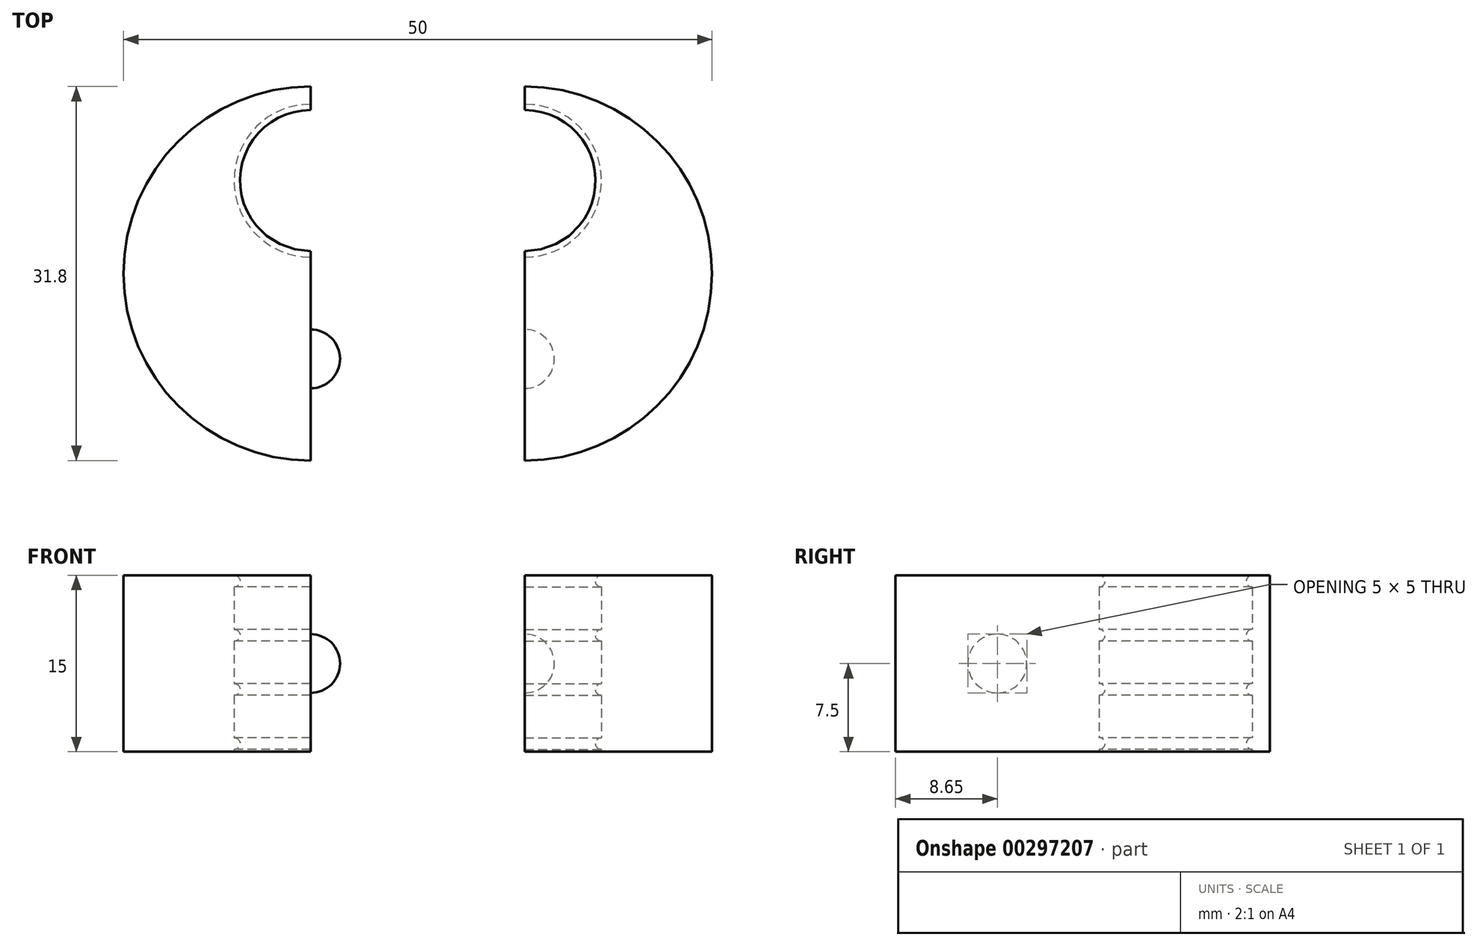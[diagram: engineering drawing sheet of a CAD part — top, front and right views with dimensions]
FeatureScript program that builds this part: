
annotation { "Feature Type Name" : "Feature", "Feature Type Description" : "" }
export const myFeature = defineFeature(function(context is Context, id is Id, definition is map)
    precondition{}
    {
        {
            var Q0;
            Q0=qCreatedBy(makeId("Top.planeOp"),FACE);
            var sketch = newSketch(context, id + "F0", { "sketchPlane" : qUnion([Q0])});
            skArc(sketch, "E0", {"start": v(-8.12, 15.9) * mm, "mid": v(-24.02, 0) * mm, "end": v(-8.12, -15.9) * mm});
            skArc(sketch, "E1", {"start": v(10.08, -15.9) * mm, "mid": v(25.98, 0) * mm, "end": v(10.08, 15.9) * mm});
            skLineSegment(sketch, "E2", {"start": v(-8.12, 15.9) * mm, "end": v(-8.12, 14.4) * mm});
            skLineSegment(sketch, "E3", {"start": v(10.08, 15.9) * mm, "end": v(10.08, 14.4) * mm});
            skArc(sketch, "E4", {"start": v(-8.12, 14.4) * mm, "mid": v(-14.62, 7.9) * mm, "end": v(-8.12, 1.4) * mm});
            skArc(sketch, "E5", {"start": v(10.08, 1.4) * mm, "mid": v(16.58, 7.9) * mm, "end": v(10.08, 14.4) * mm});
            skLineSegment(sketch, "E6.trimOffspring", {"start": v(-8.12, 1.4) * mm, "end": v(-8.12, -15.9) * mm});
            skLineSegment(sketch, "E7.trimOffspring", {"start": v(10.08, 1.4) * mm, "end": v(10.08, -15.9) * mm});
            skSolve(sketch);
        }
        {
            var Q0;
            Q0=makeQuery(id+"F0.imprint","IMPRINT",FACE,{"disambiguationData":[TD([[makeQuery(id+"F0.imprint","IMPRINT",EDGE,{"derivedFrom":sQuery(id+"F0.wireOp",EDGE,"E0")}),1.0]])]});
            var Q1;
            Q1=makeQuery(id+"F0.imprint","IMPRINT",FACE,{"disambiguationData":[TD([[makeQuery(id+"F0.imprint","IMPRINT",EDGE,{"derivedFrom":sQuery(id+"F0.wireOp",EDGE,"E1")}),1.0]])]});
            extrude(context, id + "F1", {"entities" : qUnion([Q0, Q1]), "depth" : 15 * mm});
        }
        {
            var Q0;
            Q0=makeQuery(id+"F1.opExtrude","SWEPT_FACE",FACE,{"disambiguationData":[OSD([sQuery(id+"F0.wireOp",EDGE,"E6.trimOffspring")])]});
            var sketch = newSketch(context, id + "F2", { "sketchPlane" : qUnion([Q0])});
            skArc(sketch, "E8", {"start": v(-7.25, 5) * mm, "mid": v(-4.75, 7.5) * mm, "end": v(-7.25, 10) * mm});
            skPoint(sketch, "E8.centerSnap0", {"position": v(1.4, 7.5) * mm});
            skPoint(sketch, "E8.centerSnap1", {"position": v(-7.25, 15) * mm});
            skLineSegment(sketch, "E9", {"start": v(-7.25, 10) * mm, "end": v(-7.25, 5) * mm});
            skLineSegment(sketch, "E10", {"start": v(-7.25, 15) * mm, "end": v(-7.25, 0) * mm, "construction": true});
            skSolve(sketch);
        }
        {
            var Q0;
            Q0=makeQuery(id+"F2.imprint","IMPRINT",FACE,{"disambiguationData":[TD([[makeQuery(id+"F2.imprint","IMPRINT",EDGE,{"derivedFrom":sQuery(id+"F2.wireOp",EDGE,"E8")}),1.0]])]});
            var Q1;
            Q1=sQuery(id+"F2.wireOp",EDGE,"E10");
            revolve(context, id + "F3", {"operationType" : NewBodyOperationType.ADD, "entities" : qUnion([Q0]), "axis" : qUnion([Q1]), "revolveType" : RevolveType.FULL});
        }
        {
            var Q0;
            Q0=makeQuery(id+"F1.opExtrude","SWEPT_FACE",FACE,{"disambiguationData":[OSD([sQuery(id+"F0.wireOp",EDGE,"E7.trimOffspring")])]});
            var sketch = newSketch(context, id + "F4", { "sketchPlane" : qUnion([Q0])});
            skArc(sketch, "E11", {"start": v(7.25, 10) * mm, "mid": v(4.75, 7.5) * mm, "end": v(7.25, 5) * mm});
            skPoint(sketch, "E11.centerSnap0", {"position": v(-1.4, 7.5) * mm});
            skPoint(sketch, "E11.centerSnap1", {"position": v(7.25, 0) * mm});
            skLineSegment(sketch, "E12", {"start": v(7.25, 0) * mm, "end": v(7.25, 15) * mm, "construction": true});
            skLineSegment(sketch, "E13", {"start": v(7.25, 5) * mm, "end": v(7.25, 10) * mm});
            skSolve(sketch);
        }
        {
            var Q0;
            Q0=makeQuery(id+"F4.imprint","IMPRINT",FACE,{"disambiguationData":[TD([[makeQuery(id+"F4.imprint","IMPRINT",EDGE,{"derivedFrom":sQuery(id+"F4.wireOp",EDGE,"E11")}),1.0]])]});
            var Q1;
            Q1=sQuery(id+"F4.wireOp",EDGE,"E12");
            revolve(context, id + "F5", {"operationType" : NewBodyOperationType.REMOVE, "entities" : qUnion([Q0]), "axis" : qUnion([Q1]), "revolveType" : RevolveType.FULL, "oppositeDirection" : true});
        }
        {
            var Q0;
            Q0=makeQuery(id+"F1.opExtrude","SWEPT_FACE",FACE,{"disambiguationData":[OSD([sQuery(id+"F0.wireOp",EDGE,"E6.trimOffspring")])]});
            var sketch = newSketch(context, id + "F6", { "sketchPlane" : qUnion([Q0])});
            skArc(sketch, "E14", {"start": v(1.4, 14) * mm, "mid": v(1.9, 14.5) * mm, "end": v(1.4, 15) * mm});
            skArc(sketch, "E15.1.0.0", {"start": v(1.4, 9.4) * mm, "mid": v(1.9, 9.9) * mm, "end": v(1.4, 10.4) * mm});
            skArc(sketch, "E15.2.0.0", {"start": v(1.4, 4.8) * mm, "mid": v(1.9, 5.3) * mm, "end": v(1.4, 5.8) * mm});
            skArc(sketch, "E15.3.0.0", {"start": v(1.4, 0.2) * mm, "mid": v(1.9, 0.7) * mm, "end": v(1.4, 1.2) * mm});
            skLineSegment(sketch, "E15.direction1", {"start": v(1.4, 14) * mm, "end": v(1.4, 9.4) * mm, "construction": true});
            skSolve(sketch);
        }
        {
            var Q0;
            {var subQ0=sQuery(id+"F6.wireOp",EDGE,"E14");Q0=makeQuery(id+"F6.imprint","IMPRINT",FACE,{"disambiguationData":[TD([[makeQuery(id+"F6.imprint","IMPRINT",EDGE,{"derivedFrom":subQ0}),1.0]])]});}
            var Q1;
            {var subQ0=sQuery(id+"F6.wireOp",EDGE,"E15.1.0.0");Q1=makeQuery(id+"F6.imprint","IMPRINT",FACE,{"disambiguationData":[TD([[makeQuery(id+"F6.imprint","IMPRINT",EDGE,{"derivedFrom":subQ0}),1.0]])]});}
            var Q2;
            {var subQ0=sQuery(id+"F6.wireOp",EDGE,"E15.2.0.0");Q2=makeQuery(id+"F6.imprint","IMPRINT",FACE,{"disambiguationData":[TD([[makeQuery(id+"F6.imprint","IMPRINT",EDGE,{"derivedFrom":subQ0}),1.0]])]});}
            var Q3;
            {var subQ0=sQuery(id+"F6.wireOp",EDGE,"E15.3.0.0");Q3=makeQuery(id+"F6.imprint","IMPRINT",FACE,{"disambiguationData":[TD([[makeQuery(id+"F6.imprint","IMPRINT",EDGE,{"derivedFrom":subQ0}),1.0]])]});}
            var Q4;
            Q4=makeQuery(id+"F1.opExtrude","SWEPT_FACE",FACE,{"disambiguationData":[OSD([sQuery(id+"F0.wireOp",EDGE,"E4")])]});
            revolve(context, id + "F7", {"operationType" : NewBodyOperationType.ADD, "entities" : qUnion([Q0, Q1, Q2, Q3]), "axis" : qUnion([Q4]), "revolveType" : RevolveType.ONE_DIRECTION, "oppositeDirection" : true, "angle" : 180 * degree});
        }
        {
            var Q0;
            Q0=makeQuery(id+"F1.opExtrude","SWEPT_FACE",FACE,{"disambiguationData":[OSD([sQuery(id+"F0.wireOp",EDGE,"E7.trimOffspring")])]});
            var sketch = newSketch(context, id + "F8", { "sketchPlane" : qUnion([Q0])});
            skArc(sketch, "E16", {"start": v(-1.4, 15) * mm, "mid": v(-1.9, 14.5) * mm, "end": v(-1.4, 14) * mm});
            skArc(sketch, "E17.0.1.0", {"start": v(-1.4, 10.4) * mm, "mid": v(-1.9, 9.9) * mm, "end": v(-1.4, 9.4) * mm});
            skArc(sketch, "E17.0.2.0", {"start": v(-1.4, 5.8) * mm, "mid": v(-1.9, 5.3) * mm, "end": v(-1.4, 4.8) * mm});
            skArc(sketch, "E17.0.3.0", {"start": v(-1.4, 1.2) * mm, "mid": v(-1.9, 0.7) * mm, "end": v(-1.4, 0.2) * mm});
            skArc(sketch, "E17.1.0.0", {"start": v(23.6, 15) * mm, "mid": v(23.1, 14.5) * mm, "end": v(23.6, 14) * mm});
            skArc(sketch, "E17.1.1.0", {"start": v(23.6, 10.4) * mm, "mid": v(23.1, 9.9) * mm, "end": v(23.6, 9.4) * mm});
            skArc(sketch, "E17.1.2.0", {"start": v(23.6, 5.8) * mm, "mid": v(23.1, 5.3) * mm, "end": v(23.6, 4.8) * mm});
            skArc(sketch, "E17.1.3.0", {"start": v(23.6, 1.2) * mm, "mid": v(23.1, 0.7) * mm, "end": v(23.6, 0.2) * mm});
            skArc(sketch, "E17.2.0.0", {"start": v(48.6, 15) * mm, "mid": v(48.1, 14.5) * mm, "end": v(48.6, 14) * mm});
            skArc(sketch, "E17.2.1.0", {"start": v(48.6, 10.4) * mm, "mid": v(48.1, 9.9) * mm, "end": v(48.6, 9.4) * mm});
            skArc(sketch, "E17.2.2.0", {"start": v(48.6, 5.8) * mm, "mid": v(48.1, 5.3) * mm, "end": v(48.6, 4.8) * mm});
            skArc(sketch, "E17.2.3.0", {"start": v(48.6, 1.2) * mm, "mid": v(48.1, 0.7) * mm, "end": v(48.6, 0.2) * mm});
            skLineSegment(sketch, "E17.direction1", {"start": v(-1.4, 14) * mm, "end": v(23.6, 14) * mm, "construction": true});
            skLineSegment(sketch, "E17.direction2", {"start": v(-1.4, 14) * mm, "end": v(-1.4, 9.4) * mm, "construction": true});
            skSolve(sketch);
        }
        {
            var Q0;
            {var subQ0=sQuery(id+"F8.wireOp",EDGE,"E16");Q0=makeQuery(id+"F8.imprint","IMPRINT",FACE,{"disambiguationData":[TD([[makeQuery(id+"F8.imprint","IMPRINT",EDGE,{"derivedFrom":subQ0}),1.0]])]});}
            var Q1;
            {var subQ0=sQuery(id+"F8.wireOp",EDGE,"E17.0.1.0");Q1=makeQuery(id+"F8.imprint","IMPRINT",FACE,{"disambiguationData":[TD([[makeQuery(id+"F8.imprint","IMPRINT",EDGE,{"derivedFrom":subQ0}),1.0]])]});}
            var Q2;
            {var subQ0=sQuery(id+"F8.wireOp",EDGE,"E17.0.2.0");Q2=makeQuery(id+"F8.imprint","IMPRINT",FACE,{"disambiguationData":[TD([[makeQuery(id+"F8.imprint","IMPRINT",EDGE,{"derivedFrom":subQ0}),1.0]])]});}
            var Q3;
            {var subQ0=sQuery(id+"F8.wireOp",EDGE,"E17.0.3.0");Q3=makeQuery(id+"F8.imprint","IMPRINT",FACE,{"disambiguationData":[TD([[makeQuery(id+"F8.imprint","IMPRINT",EDGE,{"derivedFrom":subQ0}),1.0]])]});}
            var Q4;
            Q4=makeQuery(id+"F1.opExtrude","SWEPT_FACE",FACE,{"disambiguationData":[OSD([sQuery(id+"F0.wireOp",EDGE,"E5")])]});
            revolve(context, id + "F9", {"operationType" : NewBodyOperationType.ADD, "entities" : qUnion([Q0, Q1, Q2, Q3]), "axis" : qUnion([Q4]), "revolveType" : RevolveType.ONE_DIRECTION, "angle" : 180 * degree});
        }
    });
